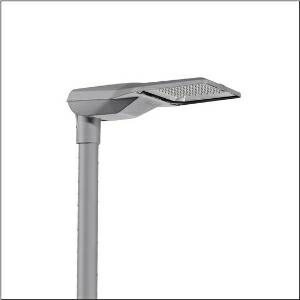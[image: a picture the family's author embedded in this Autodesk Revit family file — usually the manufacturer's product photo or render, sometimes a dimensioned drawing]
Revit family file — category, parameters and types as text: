
# Revit family: streetlight_sl_21_iq_midi___pc-r_5xe3g41g08mb_0911
name_source: partatom
category: Lighting Fixtures
units: mm (PartAtom-declared; Revit-internal decimal feet)

## family parameters
Cut with Voids When Loaded = No
Host = Face
Light Source = No
Part Type = Normal
Room Calculation Point = No
Round Connector Dimension = Use Diameter
Shared = No

## types (1)
- --- (1 x LED, 19370 lm, 146.7 W, 4000K)
    Apparent Load = 147 VA
    CIE Flux Codes = 38 78 98 100 100
    Color Rendering = 70
    Color Temperature = 4000K
    Default Elevation = 1800 mm
    Description = Streetlight SL 21 iQ midi, mast luminaire, primary light control with lens, of PMMA, primary optical cover: cover, of toughened safety glass, transparent, light distribution: PC-R, light emission: direct distribution, primary light characteristic: asymmetric, right, installation type: post-top, side-entry, LED, High Power LED, rated luminous flux: 19.370lm, luminous efficacy: 132lm/W, light colour: 740, colour temperature: 4000K, control gear: iQ Street-Remote, control: Street-Remote, Auto-Match, Temp-Guard, Lumen-Switch, Night-Set, Smart-Wire, Light-Fading, Desk-Remote (wireless, voltage-free reading and setting of iQ features in the workshop via application-optimized NFC function/RFID function), optimised constant luminous flux control (CLO 2.0), pre-setting: linear dimming characteristic, mains connection: 230..240V, AC, 50/60Hz, start of lifetime: 147W, end of service life: 161W, reduction: 62W, luminaire housing, of diecast aluminium, powder-coated, Siteco® metallic grey (DB 702S), corrosivity category C5 mid according to DIN EN ISO 12944, please order mast flange separately, inclination adjustable: 0°, 5°, 10°, 15°, sealing non-destructively replaceable, multi-level sealing system, length: 644mm, width: 335mm, height: 110mm, mast flange for spigot size: 42mm (side-entry): 5XC10008XM4, 60/48mm (side-entry/post-top): 5XC10108XM2, 76/60mm (side-entry/post-top): 5XC10108XM1, mounting height: 4..8m, protection rating (complete): IP66, insulation class (complete): insulation class II (safety insulation), certification: CE, ENEC, ENEC+, VDE, impact resistance: IK10, permissible operating ambient temperature for outdoor applications: -40..+50°C, standard-compliant lighting for roads and squares, packaging unit: 1 piece

Light Distribution: PC-R
    Height = 111 mm
    Lamp = 1 x LED
    Lamp Light Flux = 19370 lm
    Lamp Power = 146.7 W
    Lamp count = 1
    Length = 644 mm
    Luminous efficacy = 132 lm/W
    Manufacturer = Siteco
    ModVariant = No
    Model = 5XE3G41G08MB
    Number of Poles = 1
    OnlyDefault = Yes
    Power Factor = 1
    Product Name = Streetlight SL 21 iQ midi | PC-R
    Product group = mast luminaire | pylon top
    ProductGroupID = 6100
    Protection Class = Protection class II
    Protection Degree = IP 66
    RLX_Detail_Level = 1
    RLX_Emergency_Light_Flux = 0 lm
    RLX_Emergency_Type = 0
    RLX_Emergency_Type_DB = No
    RlxData = <blob elided: 29453 chars, md5=4a0fcb98>
    Socket = socket
    Standby Power = 0 W
    System Light Flux = 19370 lm
    System Power = 147 W
    Type Comments = factory setting: luminous flux: 100 % | dim-lin: 254 | 753 mA
    Type Image = l_1004298.jpg
    URL = http://relux.com
    VarID = @adj_064236
    Voltage = 0 V
    Weight = 0.00 kg
    Width = 336 mm

## geometry (parser evidence)
native form markers: Blend x4, Sweep x10
no freeform markers — native parametric forms only
